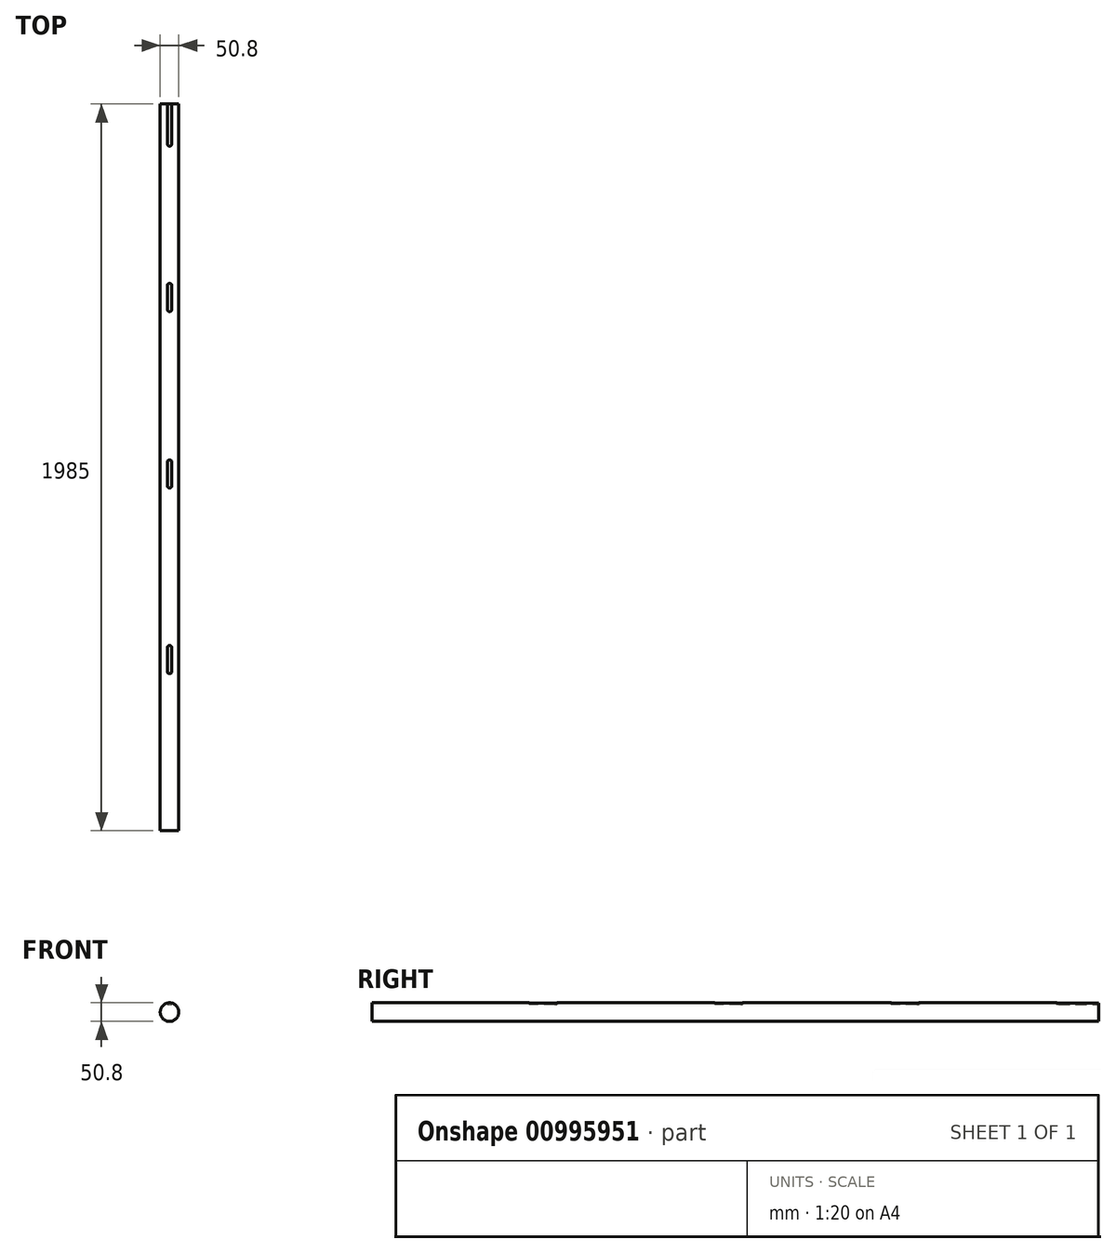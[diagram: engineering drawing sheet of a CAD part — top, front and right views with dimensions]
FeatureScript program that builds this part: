
annotation { "Feature Type Name" : "Feature", "Feature Type Description" : "" }
export const myFeature = defineFeature(function(context is Context, id is Id, definition is map)
    precondition{}
    {
        {
            var Q0;
            Q0=qCreatedBy(makeId("Front.planeOp"),FACE);
            var sketch = newSketch(context, id + "F0", { "sketchPlane" : qUnion([Q0])});
            skCircle(sketch, "E0", {"center": v(0, 0) * mm, "radius": 25.4 * mm});
            skSolve(sketch);
        }
        {
            var Q0;
            Q0 = qSketchRegion(id + "F0", true);
            extrude(context, id + "F1", {"entities" : qUnion([Q0]), "depth" : 1985 * mm, "offsetDistance" : 25.4 * mm});
        }
        {
            var Q0;
            Q0=makeQuery(id+"F1.opExtrude","CAP_FACE",FACE,{"disambiguationData":[OSD([sQuery(id+"F0.wireOp",EDGE,"E0")])],"isStart":true});
            var sketch = newSketch(context, id + "F2", { "sketchPlane" : qUnion([Q0])});
            skLineSegment(sketch, "E1.bottom", {"start": v(-6.25, 25.4) * mm, "end": v(6.25, 25.4) * mm});
            skLineSegment(sketch, "E1.top", {"start": v(-6.25, 20.4) * mm, "end": v(6.25, 20.4) * mm});
            skLineSegment(sketch, "E1.left", {"start": v(-6.25, 25.4) * mm, "end": v(-6.25, 20.4) * mm});
            skLineSegment(sketch, "E1.right", {"start": v(6.25, 25.4) * mm, "end": v(6.25, 20.4) * mm});
            skLineSegment(sketch, "E2", {"start": v(0, 0) * mm, "end": v(0, 28.15) * mm});
            skSolve(sketch);
        }
        {
            var Q0;
            Q0 = qSketchRegion(id + "F2", true);
            extrude(context, id + "F3", {"entities" : qUnion([Q0]), "operationType" : NewBodyOperationType.REMOVE, "oppositeDirection" : true, "depth" : 115 * mm - 6.25 * mm, "offsetDistance" : 25.4 * mm});
        }
        {
            var Q0;
            Q0=makeQuery(id+"F3.boolean.opBoolean","COPY",FACE,{"derivedFrom":makeQuery(id+"F3.opExtrude","SWEPT_FACE",FACE,{"disambiguationData":[OSD([sQuery(id+"F2.wireOp",EDGE,"E1.top")])]})});
            var sketch = newSketch(context, id + "F4", { "sketchPlane" : qUnion([Q0])});
            skArc(sketch, "E3", {"start": v(-6.25, -108.75) * mm, "mid": v(0, -115) * mm, "end": v(6.25, -108.75) * mm});
            skLineSegment(sketch, "E4", {"start": v(-6.25, -108.75) * mm, "end": v(6.25, -108.75) * mm});
            skSolve(sketch);
        }
        {
            var Q0;
            Q0 = qSketchRegion(id + "F4", true);
            extrude(context, id + "F5", {"entities" : qUnion([Q0]), "operationType" : NewBodyOperationType.REMOVE, "depth" : 2463.8 * mm, "offsetDistance" : 25.4 * mm});
        }
        {
            var Q0;
            Q0=makeQuery(id+"F5.boolean.opBoolean","MERGE",FACE,{"derivedFrom":[makeQuery(id+"F3.boolean.opBoolean","COPY",FACE,{"derivedFrom":makeQuery(id+"F3.opExtrude","SWEPT_FACE",FACE,{"disambiguationData":[OSD([sQuery(id+"F2.wireOp",EDGE,"E1.top")])]})})],"fromTools":[makeQuery(id+"F5.opExtrude","CAP_FACE",FACE,{"disambiguationData":[OSD([sQuery(id+"F4.wireOp",EDGE,"E3"),sQuery(id+"F4.wireOp",EDGE,"E4")])],"isStart":true})]});
            var sketch = newSketch(context, id + "F6", { "sketchPlane" : qUnion([Q0])});
            skLineSegment(sketch, "E5", {"start": v(-6.25, -496.25) * mm, "end": v(-6.25, -560.75) * mm});
            skLineSegment(sketch, "E6", {"start": v(6.25, -496.25) * mm, "end": v(6.25, -560.75) * mm});
            skArc(sketch, "E7", {"start": v(6.25, -496.25) * mm, "mid": v(0, -490) * mm, "end": v(-6.25, -496.25) * mm});
            skArc(sketch, "E8", {"start": v(-6.25, -560.75) * mm, "mid": v(0, -567) * mm, "end": v(6.25, -560.75) * mm});
            skLineSegment(sketch, "E9", {"start": v(-6.25, -978.25) * mm, "end": v(-6.25, -1042.75) * mm});
            skLineSegment(sketch, "E10", {"start": v(6.25, -978.25) * mm, "end": v(6.25, -1042.75) * mm});
            skArc(sketch, "E11", {"start": v(6.25, -978.25) * mm, "mid": v(0, -972) * mm, "end": v(-6.25, -978.25) * mm});
            skArc(sketch, "E12", {"start": v(-6.25, -1042.75) * mm, "mid": v(0, -1049) * mm, "end": v(6.25, -1042.75) * mm});
            skLineSegment(sketch, "E13", {"start": v(-6.25, -1485.25) * mm, "end": v(-6.25, -1549.75) * mm});
            skLineSegment(sketch, "E14", {"start": v(6.25, -1485.25) * mm, "end": v(6.25, -1549.75) * mm});
            skArc(sketch, "E15", {"start": v(6.25, -1485.25) * mm, "mid": v(0, -1479) * mm, "end": v(-6.25, -1485.25) * mm});
            skArc(sketch, "E16", {"start": v(-6.25, -1549.75) * mm, "mid": v(0, -1556) * mm, "end": v(6.25, -1549.75) * mm});
            skSolve(sketch);
        }
        {
            var Q0;
            Q0 = qSketchRegion(id + "F6", true);
            extrude(context, id + "F7", {"entities" : qUnion([Q0]), "operationType" : NewBodyOperationType.REMOVE, "depth" : 127 * mm, "offsetDistance" : 25 * mm});
        }
    });
